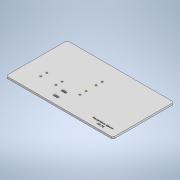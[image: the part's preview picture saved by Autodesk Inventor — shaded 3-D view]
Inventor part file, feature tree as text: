
AUTODESK INVENTOR PART (.ipt)
format: ipt  version: 2022 (Build 260153000, 153)  size: 146,432 bytes
history: native  units: mm
features: sketch x3, extrude x2, fillet x1, hole x1
ambient origin geometry x8: Origin, YZ Plane, XZ Plane, XY Plane, X Axis, Y Axis, Z Axis, Center Point
bodies: Solid1 (feature_tree)
feature tree (7):
  extrude  "Extrusion1"  Depth=200.0mm
  fillet  "Fillet1"  Radius=6.0mm
  sketch  "Sketch2"  dims[d4=5.0mm d7=20.0mm]
  sketch  "Sketch3"  dims[d8=20.0mm d11=5.4mm d12=6.0mm d13=4.0mm d14=2.0mm d15=90.0deg d16=8.0mm d17=20.594885mm d18=20.0mm d19=20.0mm d20=50.0mm d21=58.5mm d22=55.0mm d23=60.0mm d24=33.0mm d25=15.0mm d26=6.0mm d27=35.0mm d28=0.0mm d29=0.0mm d30=50.0mm d31=15.0mm d32=6.0mm d33=35.0mm d34=20.0mm]
  hole  "Hole1"  [1 undecoded]
  extrude  "Extrusion2"  Depth=20.0mm
  sketch  "Sketch1"  dims[d0=350.0mm d1=200.0mm d2=6.0mm d3=0.0mm]
note: 1 required parameter value undecoded (feature->parameter linkage not recoverable at this tier; creation-order binding heuristic only, values carry confidence <= 0.55)
